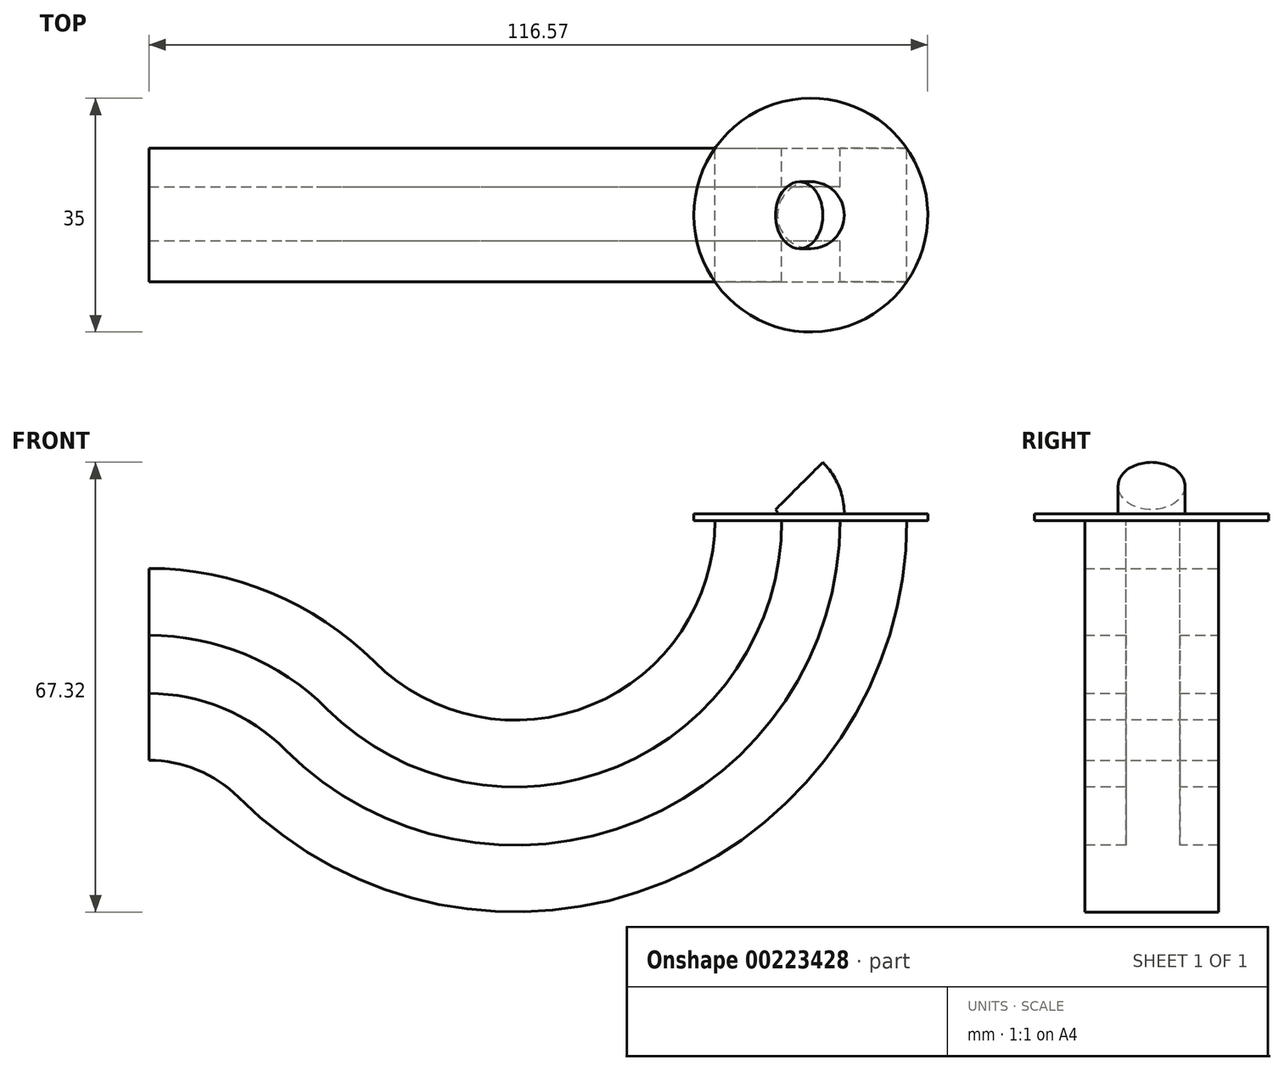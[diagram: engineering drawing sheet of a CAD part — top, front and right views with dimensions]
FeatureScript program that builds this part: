
annotation { "Feature Type Name" : "Feature", "Feature Type Description" : "" }
export const myFeature = defineFeature(function(context is Context, id is Id, definition is map)
    precondition{}
    {
        {
            var Q0;
            Q0=qCreatedBy(makeId("Top.planeOp"),FACE);
            var sketch = newSketch(context, id + "F0", { "sketchPlane" : qUnion([Q0])});
            skCircle(sketch, "E0", {"center": v(17.26, 39.95) * mm, "radius": 5 * mm});
            skLineSegment(sketch, "E1", {"start": v(11.34, 46.2) * mm, "end": v(11.34, 31.4) * mm});
            skSolve(sketch);
        }
        {
            var Q0;
            Q0=makeQuery(id+"F0.imprint","IMPRINT",FACE,{"disambiguationData":[TD([[makeQuery(id+"F0.imprint","IMPRINT",EDGE,{"derivedFrom":sQuery(id+"F0.wireOp",EDGE,"E0")}),1.0]])]});
            var Q1;
            Q1=sQuery(id+"F0.wireOp",EDGE,"E1");
            revolve(context, id + "F1", {"entities" : qUnion([Q0]), "axis" : qUnion([Q1]), "revolveType" : RevolveType.TWO_DIRECTIONS, "angle" : 45 * degree, "angleBack" : 360 * degree});
        }
        {
            var Q0;
            Q0=makeQuery(id+"F1.opRevolve","CAP_FACE",FACE,{"disambiguationData":[OSD([sQuery(id+"F0.wireOp",EDGE,"E0")])],"isStart":true});
            var sketch = newSketch(context, id + "F2", { "sketchPlane" : qUnion([Q0])});
            skCircle(sketch, "E2", {"center": v(17.26, -39.95) * mm, "radius": 17.5 * mm});
            skSolve(sketch);
        }
        {
            var Q0;
            Q0=makeQuery(id+"F2.imprint","IMPRINT",FACE,{"disambiguationData":[TD([[makeQuery(id+"F2.imprint","IMPRINT",EDGE,{"derivedFrom":sQuery(id+"F2.wireOp",EDGE,"E2")}),1.0]])]});
            var Q1;
            Q1=makeQuery(id+"F2.imprint","IMPRINT",FACE,{"disambiguationData":[TD([[makeQuery(id+"F2.imprint","IMPRINT",EDGE,{"derivedFrom":makeQuery(id+"F1.opRevolve","CAP_EDGE",EDGE,{"disambiguationData":[OSD([sQuery(id+"F0.wireOp",EDGE,"E0")])],"isStart":true})}),-1.0]])]});
            extrude(context, id + "F3", {"entities" : qUnion([Q0, Q1]), "operationType" : NewBodyOperationType.ADD, "depth" : 1 * mm});
        }
        {
            var Q0;
            Q0=makeQuery(id+"F3.opExtrude","CAP_FACE",FACE,{"disambiguationData":[OSD([sQuery(id+"F2.wireOp",EDGE,"E2")])],"isStart":false});
            var sketch = newSketch(context, id + "F4", { "sketchPlane" : qUnion([Q0])});
            skLineSegment(sketch, "E3", {"start": v(2.9, -29.95) * mm, "end": v(2.9, -49.95) * mm});
            skLineSegment(sketch, "E4", {"start": v(2.9, -49.95) * mm, "end": v(12.9, -49.95) * mm});
            skLineSegment(sketch, "E5", {"start": v(12.9, -29.95) * mm, "end": v(2.9, -29.95) * mm});
            skPoint(sketch, "E6.middle", {"position": v(17.26, -39.95) * mm});
            skLineSegment(sketch, "E7.bottom", {"start": v(31.62, -29.95) * mm, "end": v(21.62, -29.95) * mm});
            skLineSegment(sketch, "E7.top", {"start": v(31.62, -49.95) * mm, "end": v(21.62, -49.95) * mm});
            skPoint(sketch, "E8", {"position": v(12.9, -36.12) * mm});
            skPoint(sketch, "E9", {"position": v(21.62, -36.12) * mm});
            skPoint(sketch, "E10", {"position": v(12.9, -44.18) * mm});
            skPoint(sketch, "E11", {"position": v(21.62, -44.18) * mm});
            skLineSegment(sketch, "E12", {"start": v(12.9, -44.18) * mm, "end": v(12.9, -49.95) * mm});
            skLineSegment(sketch, "E13", {"start": v(21.62, -29.95) * mm, "end": v(21.62, -36.12) * mm});
            skLineSegment(sketch, "E14", {"start": v(21.62, -44.18) * mm, "end": v(21.62, -49.95) * mm});
            skLineSegment(sketch, "E15", {"start": v(31.62, -29.95) * mm, "end": v(31.62, -49.95) * mm});
            skLineSegment(sketch, "E16", {"start": v(-26.97, -25.42) * mm, "end": v(-26.97, -55.55) * mm});
            skLineSegment(sketch, "E17", {"start": v(12.9, -29.95) * mm, "end": v(12.9, -36.12) * mm});
            skLineSegment(sketch, "E18", {"start": v(12.9, -36.12) * mm, "end": v(21.62, -36.12) * mm});
            skLineSegment(sketch, "E19", {"start": v(21.62, -44.18) * mm, "end": v(12.9, -44.18) * mm});
            skSolve(sketch);
        }
        {
            var Q0;
            Q0=makeQuery(id+"F4.imprint","IMPRINT",FACE,{"disambiguationData":[TD([[makeQuery(id+"F4.imprint","IMPRINT",EDGE,{"derivedFrom":sQuery(id+"F4.wireOp",EDGE,"E3")}),1.0]])]});
            var Q1;
            Q1=makeQuery(id+"F4.imprint","IMPRINT",FACE,{"disambiguationData":[TD([[makeQuery(id+"F4.imprint","IMPRINT",EDGE,{"derivedFrom":sQuery(id+"F4.wireOp",EDGE,"E7.bottom")}),1.0]])]});
            var Q2;
            Q2=sQuery(id+"F4.wireOp",EDGE,"E16");
            revolve(context, id + "F5", {"operationType" : NewBodyOperationType.ADD, "entities" : qUnion([Q0, Q1]), "axis" : qUnion([Q2]), "revolveType" : RevolveType.ONE_DIRECTION, "angle" : 135 * degree});
        }
        {
            var Q0;
            Q0=makeQuery(id+"F5.opRevolve","CAP_FACE",FACE,{"disambiguationData":[OSD([sQuery(id+"F4.wireOp",EDGE,"E3"),sQuery(id+"F4.wireOp",EDGE,"E4"),sQuery(id+"F4.wireOp",EDGE,"E5"),sQuery(id+"F4.wireOp",EDGE,"E7.bottom"),sQuery(id+"F4.wireOp",EDGE,"E7.top"),sQuery(id+"F4.wireOp",EDGE,"8fVzqQoe-QOPs-ZCh5-ai9C-A4RtrGaLOi3c"),sQuery(id+"F4.wireOp",EDGE,"dCLopN7q-dHg6-Dtuh-PpNe-Q6AOM9fsKLdI"),sQuery(id+"F4.wireOp",EDGE,"nyfnzoNK-QgQO-hLSM-gTAi-vVS44sqsABuP"),sQuery(id+"F4.wireOp",EDGE,"E12"),sQuery(id+"F4.wireOp",EDGE,"E13"),sQuery(id+"F4.wireOp",EDGE,"E14"),sQuery(id+"F4.wireOp",EDGE,"E15")])],"isStart":false});
            var sketch = newSketch(context, id + "F6", { "sketchPlane" : qUnion([Q0])});
            skLineSegment(sketch, "E20", {"start": v(-20.63, -97.33) * mm, "end": v(-64.1, -97.33) * mm});
            skSolve(sketch);
        }
        {
            var Q0;
            Q0=makeQuery(id+"F6.imprint","IMPRINT",FACE,{"disambiguationData":[TD([[makeQuery(id+"F6.imprint","IMPRINT",EDGE,{"derivedFrom":makeQuery(id+"F5.opRevolve","CAP_EDGE",EDGE,{"disambiguationData":[OSD([sQuery(id+"F4.wireOp",EDGE,"E3")])],"isStart":false})}),1.0]])]});
            var Q1;
            Q1=sQuery(id+"F6.wireOp",EDGE,"E20");
            revolve(context, id + "F7", {"operationType" : NewBodyOperationType.ADD, "entities" : qUnion([Q0]), "axis" : qUnion([Q1]), "revolveType" : RevolveType.ONE_DIRECTION, "oppositeDirection" : true, "angle" : 45 * degree});
        }
    });
